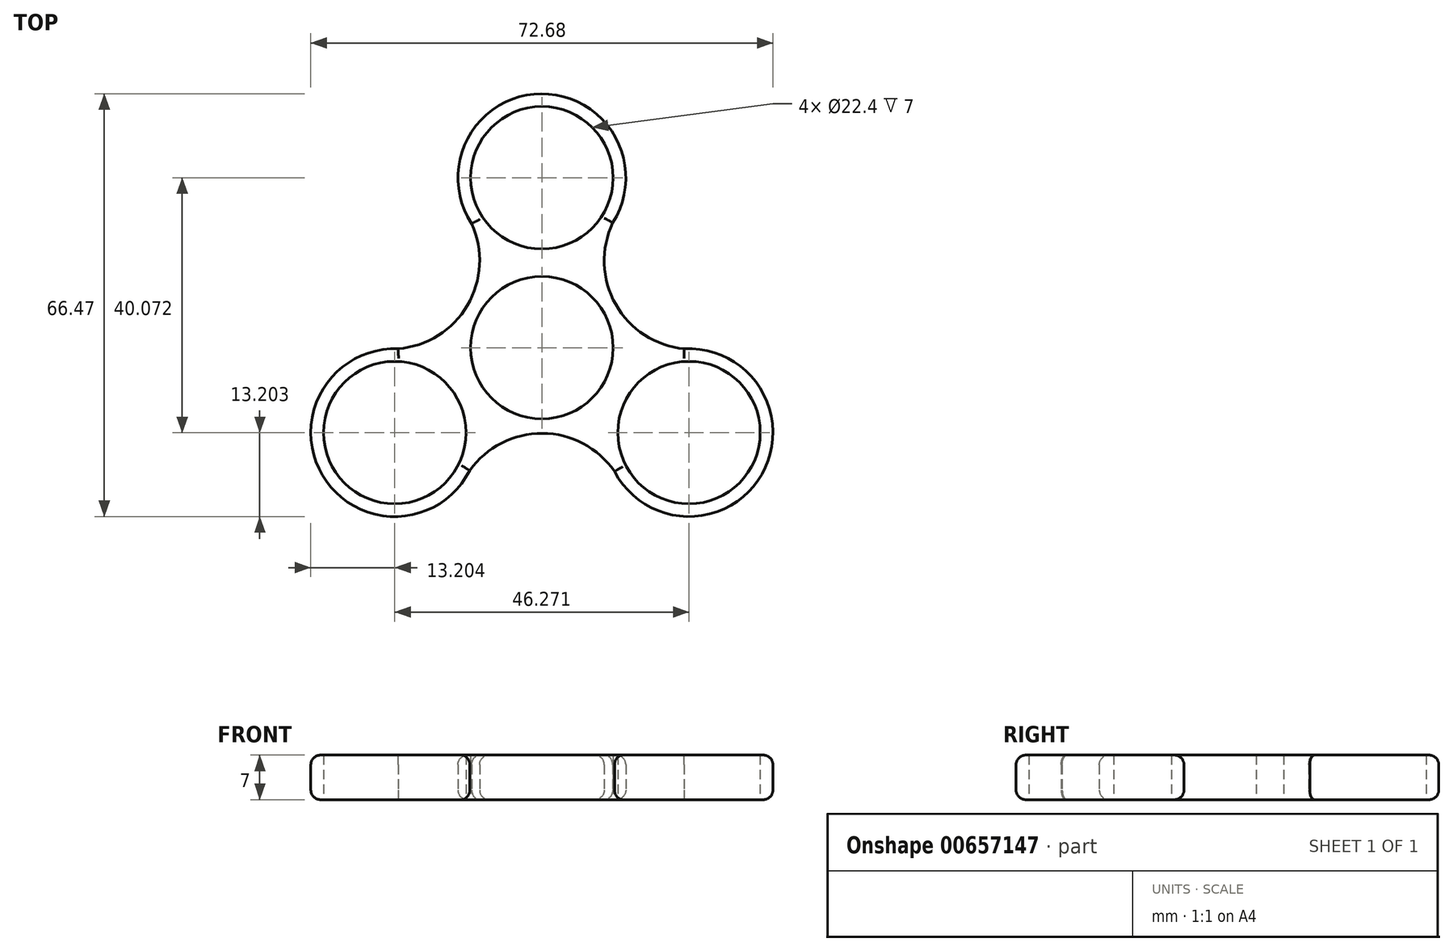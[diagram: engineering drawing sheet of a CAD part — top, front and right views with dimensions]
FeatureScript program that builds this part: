
annotation { "Feature Type Name" : "Feature", "Feature Type Description" : "" }
export const myFeature = defineFeature(function(context is Context, id is Id, definition is map)
    precondition{}
    {
        {
            var Q0;
            Q0=qCreatedBy(makeId("Top.planeOp"),FACE);
            var sketch = newSketch(context, id + "F0", { "sketchPlane" : qUnion([Q0])});
            skCircle(sketch, "E0", {"center": v(0, 0) * mm, "radius": 11.2 * mm});
            skArc(sketch, "E1", {"start": v(11.14, 19.64) * mm, "mid": v(-0.09, 39.91) * mm, "end": v(-11.04, 19.49) * mm});
            skCircle(sketch, "E2", {"center": v(0, 26.71) * mm, "radius": 11.2 * mm});
            skCircle(sketch, "E3.1.0", {"center": v(-23.14, -13.36) * mm, "radius": 11.2 * mm});
            skArc(sketch, "E3.1.1", {"start": v(-22.58, -0.17) * mm, "mid": v(-34.52, -20.04) * mm, "end": v(-11.35, -19.3) * mm});
            skCircle(sketch, "E3.2.0", {"center": v(23.14, -13.36) * mm, "radius": 11.2 * mm});
            skArc(sketch, "E3.2.1", {"start": v(11.44, -19.47) * mm, "mid": v(34.61, -19.88) * mm, "end": v(22.4, -0.18) * mm});
            skArc(sketch, "E4", {"start": v(11.14, 19.64) * mm, "mid": v(11.62, 6.8) * mm, "end": v(22.4, -0.18) * mm});
            skArc(sketch, "E5.1.0", {"start": v(-22.58, -0.17) * mm, "mid": v(-11.7, 6.66) * mm, "end": v(-11.04, 19.49) * mm});
            skArc(sketch, "E5.2.0", {"start": v(11.44, -19.47) * mm, "mid": v(0.08, -13.47) * mm, "end": v(-11.35, -19.3) * mm});
            skSolve(sketch);
        }
        {
            var Q0;
            Q0=makeQuery(id+"F0.imprint","IMPRINT",FACE,{"disambiguationData":[TD([[makeQuery(id+"F0.imprint","IMPRINT",EDGE,{"derivedFrom":sQuery(id+"F0.wireOp",EDGE,"E0")}),-1.0]])]});
            extrude(context, id + "F1", {"entities" : qUnion([Q0]), "depth" : 7 * mm, "offsetDistance" : 25 * mm});
        }
        {
            var Q0;
            Q0=makeQuery(id+"F1.opExtrude","CAP_EDGE",EDGE,{"disambiguationData":[OSD([sQuery(id+"F0.wireOp",EDGE,"E3.1.1")])],"isStart":false});
            var Q1;
            Q1=makeQuery(id+"F1.opExtrude","CAP_EDGE",EDGE,{"disambiguationData":[OSD([sQuery(id+"F0.wireOp",EDGE,"E5.1.0")])],"isStart":false});
            var Q2;
            Q2=makeQuery(id+"F1.opExtrude","CAP_EDGE",EDGE,{"disambiguationData":[OSD([sQuery(id+"F0.wireOp",EDGE,"E3.2.1")])],"isStart":false});
            var Q3;
            Q3=makeQuery(id+"F1.opExtrude","CAP_EDGE",EDGE,{"disambiguationData":[OSD([sQuery(id+"F0.wireOp",EDGE,"E3.2.1")])],"isStart":true});
            var Q4;
            Q4=makeQuery(id+"F1.opExtrude","CAP_EDGE",EDGE,{"disambiguationData":[OSD([sQuery(id+"F0.wireOp",EDGE,"E5.2.0")])],"isStart":true});
            var Q5;
            Q5=makeQuery(id+"F1.opExtrude","CAP_EDGE",EDGE,{"disambiguationData":[OSD([sQuery(id+"F0.wireOp",EDGE,"E3.1.1")])],"isStart":true});
            var Q6;
            Q6=makeQuery(id+"F1.opExtrude","CAP_EDGE",EDGE,{"disambiguationData":[OSD([sQuery(id+"F0.wireOp",EDGE,"E1")])],"isStart":false});
            var Q7;
            Q7=makeQuery(id+"F1.opExtrude","CAP_EDGE",EDGE,{"disambiguationData":[OSD([sQuery(id+"F0.wireOp",EDGE,"E1")])],"isStart":true});
            var Q8;
            Q8=makeQuery(id+"F1.opExtrude","CAP_EDGE",EDGE,{"disambiguationData":[OSD([sQuery(id+"F0.wireOp",EDGE,"E4")])],"isStart":true});
            var Q9;
            Q9=makeQuery(id+"F1.opExtrude","CAP_EDGE",EDGE,{"disambiguationData":[OSD([sQuery(id+"F0.wireOp",EDGE,"E5.1.0")])],"isStart":true});
            var Q10;
            Q10=makeQuery(id+"F1.opExtrude","CAP_EDGE",EDGE,{"disambiguationData":[OSD([sQuery(id+"F0.wireOp",EDGE,"E5.2.0")])],"isStart":false});
            var Q11;
            Q11=makeQuery(id+"F1.opExtrude","CAP_EDGE",EDGE,{"disambiguationData":[OSD([sQuery(id+"F0.wireOp",EDGE,"E4")])],"isStart":false});
            fillet(context, id + "F2", {"entities" : qUnion([Q0, Q1, Q2, Q3, Q4, Q5, Q6, Q7, Q8, Q9, Q10, Q11]), "radius" : 1.5 * mm, "allowEdgeOverflow" : false});
        }
    });
